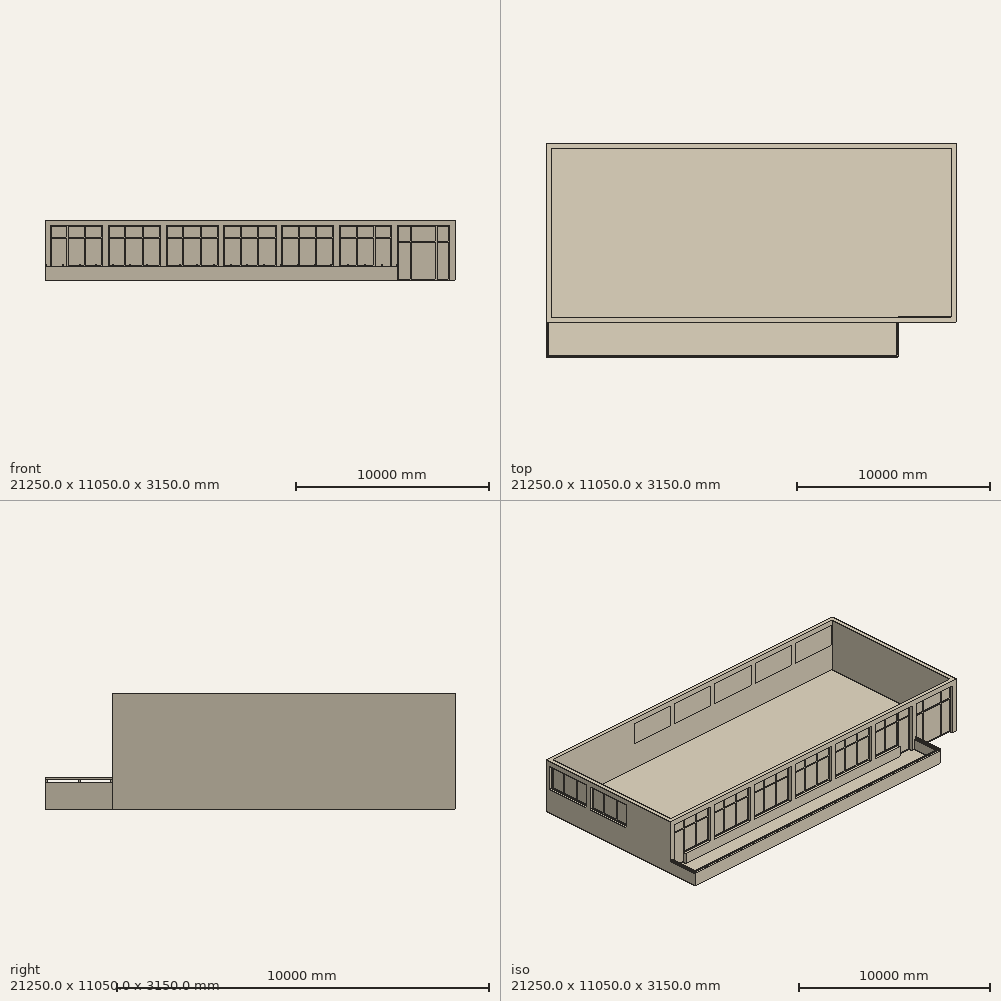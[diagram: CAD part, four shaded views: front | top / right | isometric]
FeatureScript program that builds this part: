
annotation { "Feature Type Name" : "Feature", "Feature Type Description" : "" }
export const myFeature = defineFeature(function(context is Context, id is Id, definition is map)
    precondition{}
    {
        {
            var Q0;
            Q0=qCreatedBy(makeId("Top.planeOp"),FACE);
            var sketch = newSketch(context, id + "F0", { "sketchPlane" : qUnion([Q0])});
            skLineSegment(sketch, "E0.bottom", {"start": v(0, 0) * mm, "end": v(21250, 0) * mm});
            skLineSegment(sketch, "E0.top", {"start": v(0, -9250) * mm, "end": v(21250, -9250) * mm});
            skLineSegment(sketch, "E0.left", {"start": v(0, 0) * mm, "end": v(0, -9250) * mm});
            skLineSegment(sketch, "E0.right", {"start": v(21250, 0) * mm, "end": v(21250, -9250) * mm});
            skSolve(sketch);
        }
        {
            var Q0;
            Q0=qSketchRegion(id+"F0",true);
            extrude(context, id + "F1", {"entities" : qUnion([Q0]), "depth" : 150 * mm, "offsetDistance" : 25 * mm});
        }
        {
            var Q0;
            Q0=makeQuery(id+"F1.opExtrude","CAP_FACE",FACE,{"disambiguationData":[OSD([sQuery(id+"F0.wireOp",EDGE,"E0.bottom"),sQuery(id+"F0.wireOp",EDGE,"E0.top"),sQuery(id+"F0.wireOp",EDGE,"E0.left"),sQuery(id+"F0.wireOp",EDGE,"E0.right")])],"isStart":false});
            var sketch = newSketch(context, id + "F2", { "sketchPlane" : qUnion([Q0])});
            skLineSegment(sketch, "E1.0.0", {"start": v(0, 0) * mm, "end": v(0, -9250) * mm});
            skLineSegment(sketch, "E1.0.1", {"start": v(0, -9250) * mm, "end": v(21250, -9250) * mm});
            skLineSegment(sketch, "E1.0.2", {"start": v(21250, -9250) * mm, "end": v(21250, 0) * mm});
            skLineSegment(sketch, "E1.0.3", {"start": v(21250, 0) * mm, "end": v(0, 0) * mm});
            skLineSegment(sketch, "E2.0", {"start": v(250, -250) * mm, "end": v(250, -9000) * mm});
            skLineSegment(sketch, "E2.1", {"start": v(21000, -250) * mm, "end": v(250, -250) * mm});
            skLineSegment(sketch, "E2.2", {"start": v(21000, -9000) * mm, "end": v(21000, -250) * mm});
            skLineSegment(sketch, "E2.3", {"start": v(250, -9000) * mm, "end": v(21000, -9000) * mm});
            skSolve(sketch);
        }
        {
            var Q0;
            Q0=qSketchRegion(id+"F2",true);
            extrude(context, id + "F3", {"entities" : qUnion([Q0]), "operationType" : NewBodyOperationType.ADD, "depth" : 3000 * mm, "offsetDistance" : 25 * mm});
        }
        {
            var Q0;
            Q0=makeQuery(id+"F3.boolean.opBoolean","MERGE",FACE,{"derivedFrom":[makeQuery(id+"F1.opExtrude","SWEPT_FACE",FACE,{"disambiguationData":[OSD([sQuery(id+"F0.wireOp",EDGE,"E0.top")])]}),makeQuery(id+"F3.opExtrude","SWEPT_FACE",FACE,{"disambiguationData":[OSD([sQuery(id+"F2.wireOp",EDGE,"E1.0.1")])]})]});
            var sketch = newSketch(context, id + "F4", { "sketchPlane" : qUnion([Q0])});
            skLineSegment(sketch, "E3", {"start": v(1150, 150) * mm, "end": v(250, 150) * mm});
            skLineSegment(sketch, "E4", {"start": v(250, 150) * mm, "end": v(250, 2850) * mm});
            skLineSegment(sketch, "E5", {"start": v(250, 2850) * mm, "end": v(2950, 2850) * mm});
            skLineSegment(sketch, "E6", {"start": v(2950, 2850) * mm, "end": v(2950, 750) * mm});
            skLineSegment(sketch, "E7", {"start": v(2950, 750) * mm, "end": v(1150, 750) * mm});
            skLineSegment(sketch, "E8", {"start": v(1150, 750) * mm, "end": v(1150, 150) * mm});
            skLineSegment(sketch, "E9.bottom", {"start": v(3250, 2850) * mm, "end": v(5950, 2850) * mm});
            skLineSegment(sketch, "E9.top", {"start": v(3250, 750) * mm, "end": v(5950, 750) * mm});
            skLineSegment(sketch, "E9.left", {"start": v(3250, 2850) * mm, "end": v(3250, 750) * mm});
            skLineSegment(sketch, "E9.right", {"start": v(5950, 2850) * mm, "end": v(5950, 750) * mm});
            skLineSegment(sketch, "E10.1.0.0", {"start": v(6250, 750) * mm, "end": v(8950, 750) * mm});
            skLineSegment(sketch, "E10.1.0.1", {"start": v(8950, 2850) * mm, "end": v(8950, 750) * mm});
            skLineSegment(sketch, "E10.1.0.2", {"start": v(6250, 2850) * mm, "end": v(6250, 750) * mm});
            skLineSegment(sketch, "E10.1.0.3", {"start": v(6250, 2850) * mm, "end": v(8950, 2850) * mm});
            skLineSegment(sketch, "E10.2.0.0", {"start": v(9250, 750) * mm, "end": v(11950, 750) * mm});
            skLineSegment(sketch, "E10.2.0.1", {"start": v(11950, 2850) * mm, "end": v(11950, 750) * mm});
            skLineSegment(sketch, "E10.2.0.2", {"start": v(9250, 2850) * mm, "end": v(9250, 750) * mm});
            skLineSegment(sketch, "E10.2.0.3", {"start": v(9250, 2850) * mm, "end": v(11950, 2850) * mm});
            skLineSegment(sketch, "E10.3.0.0", {"start": v(12250, 750) * mm, "end": v(14950, 750) * mm});
            skLineSegment(sketch, "E10.3.0.1", {"start": v(14950, 2850) * mm, "end": v(14950, 750) * mm});
            skLineSegment(sketch, "E10.3.0.2", {"start": v(12250, 2850) * mm, "end": v(12250, 750) * mm});
            skLineSegment(sketch, "E10.3.0.3", {"start": v(12250, 2850) * mm, "end": v(14950, 2850) * mm});
            skLineSegment(sketch, "E10.direction1", {"start": v(3250, 750) * mm, "end": v(6250, 750) * mm, "construction": true});
            skLineSegment(sketch, "E11.bottom", {"start": v(18250, 2850) * mm, "end": v(20950, 2850) * mm});
            skLineSegment(sketch, "E11.top", {"start": v(18250, 0) * mm, "end": v(20950, 0) * mm});
            skLineSegment(sketch, "E11.left", {"start": v(18250, 2850) * mm, "end": v(18250, 0) * mm});
            skLineSegment(sketch, "E11.right", {"start": v(20950, 2850) * mm, "end": v(20950, 0) * mm});
            skLineSegment(sketch, "E12", {"start": v(3250, 750) * mm, "end": v(14950, 750) * mm, "construction": true});
            skLineSegment(sketch, "E13", {"start": v(9100, 750) * mm, "end": v(9100, 3150) * mm, "construction": true});
            skLineSegment(sketch, "E14.MirrorCS", {"start": v(15250, 750) * mm, "end": v(17050, 750) * mm});
            skLineSegment(sketch, "E15.MirrorCS", {"start": v(17950, 2850) * mm, "end": v(15250, 2850) * mm});
            skLineSegment(sketch, "E16.MirrorCS", {"start": v(15250, 2850) * mm, "end": v(15250, 750) * mm});
            skLineSegment(sketch, "E17.MirrorCS", {"start": v(17050, 150) * mm, "end": v(17950, 150) * mm});
            skLineSegment(sketch, "E18.MirrorCS", {"start": v(17950, 150) * mm, "end": v(17950, 2850) * mm});
            skLineSegment(sketch, "E19.MirrorCS", {"start": v(17050, 750) * mm, "end": v(17050, 150) * mm});
            skSolve(sketch);
        }
        {
            var Q0;
            Q0=qSketchRegion(id+"F4",true);
            extrude(context, id + "F5", {"entities" : qUnion([Q0]), "operationType" : NewBodyOperationType.REMOVE, "oppositeDirection" : true, "depth" : 300 * mm, "offsetDistance" : 25 * mm});
        }
        {
            var Q0;
            Q0=makeQuery(id+"F3.opExtrude","SWEPT_FACE",FACE,{"disambiguationData":[OSD([sQuery(id+"F2.wireOp",EDGE,"E2.3")])]});
            var sketch = newSketch(context, id + "F6", { "sketchPlane" : qUnion([Q0])});
            skLineSegment(sketch, "E20.0", {"start": v(-1150, 150) * mm, "end": v(-250, 150) * mm});
            skLineSegment(sketch, "E20.1", {"start": v(-250, 150) * mm, "end": v(-250, 2850) * mm});
            skLineSegment(sketch, "E20.2", {"start": v(-250, 2850) * mm, "end": v(-2950, 2850) * mm});
            skLineSegment(sketch, "E20.3", {"start": v(-2950, 2850) * mm, "end": v(-2950, 750) * mm});
            skLineSegment(sketch, "E20.4", {"start": v(-2950, 750) * mm, "end": v(-1150, 750) * mm});
            skLineSegment(sketch, "E20.5", {"start": v(-1150, 750) * mm, "end": v(-1150, 150) * mm});
            skLineSegment(sketch, "E20.6", {"start": v(-3250, 2850) * mm, "end": v(-5950, 2850) * mm});
            skLineSegment(sketch, "E20.7", {"start": v(-3250, 750) * mm, "end": v(-5950, 750) * mm});
            skLineSegment(sketch, "E20.8", {"start": v(-3250, 2850) * mm, "end": v(-3250, 750) * mm});
            skLineSegment(sketch, "E20.9", {"start": v(-5950, 2850) * mm, "end": v(-5950, 750) * mm});
            skLineSegment(sketch, "E20.10", {"start": v(-6250, 750) * mm, "end": v(-8950, 750) * mm});
            skLineSegment(sketch, "E20.11", {"start": v(-8950, 2850) * mm, "end": v(-8950, 750) * mm});
            skLineSegment(sketch, "E20.12", {"start": v(-6250, 2850) * mm, "end": v(-6250, 750) * mm});
            skLineSegment(sketch, "E20.13", {"start": v(-6250, 2850) * mm, "end": v(-8950, 2850) * mm});
            skLineSegment(sketch, "E20.14", {"start": v(-9250, 750) * mm, "end": v(-11950, 750) * mm});
            skLineSegment(sketch, "E20.15", {"start": v(-11950, 2850) * mm, "end": v(-11950, 750) * mm});
            skLineSegment(sketch, "E20.16", {"start": v(-9250, 2850) * mm, "end": v(-9250, 750) * mm});
            skLineSegment(sketch, "E20.17", {"start": v(-9250, 2850) * mm, "end": v(-11950, 2850) * mm});
            skLineSegment(sketch, "E20.18", {"start": v(-12250, 750) * mm, "end": v(-14950, 750) * mm});
            skLineSegment(sketch, "E20.19", {"start": v(-14950, 2850) * mm, "end": v(-14950, 750) * mm});
            skLineSegment(sketch, "E20.20", {"start": v(-12250, 2850) * mm, "end": v(-12250, 750) * mm});
            skLineSegment(sketch, "E20.21", {"start": v(-12250, 2850) * mm, "end": v(-14950, 2850) * mm});
            skLineSegment(sketch, "E20.26", {"start": v(-3250, 750) * mm, "end": v(-6250, 750) * mm});
            skLineSegment(sketch, "E20.27", {"start": v(-18250, 2850) * mm, "end": v(-20950, 2850) * mm});
            skLineSegment(sketch, "E20.28", {"start": v(-18250, 0) * mm, "end": v(-20950, 0) * mm});
            skLineSegment(sketch, "E20.29", {"start": v(-18250, 2850) * mm, "end": v(-18250, 0) * mm});
            skLineSegment(sketch, "E20.30", {"start": v(-20950, 2850) * mm, "end": v(-20950, 0) * mm});
            skLineSegment(sketch, "E21.0", {"start": v(-17950, 2850) * mm, "end": v(-15250, 2850) * mm});
            skLineSegment(sketch, "E22.0", {"start": v(-15250, 2850) * mm, "end": v(-15250, 750) * mm});
            skLineSegment(sketch, "E23.0", {"start": v(-15250, 750) * mm, "end": v(-17050, 750) * mm});
            skLineSegment(sketch, "E24.0", {"start": v(-17050, 750) * mm, "end": v(-17050, 150) * mm});
            skLineSegment(sketch, "E25.0", {"start": v(-17050, 150) * mm, "end": v(-17950, 150) * mm});
            skLineSegment(sketch, "E26.0", {"start": v(-17950, 150) * mm, "end": v(-17950, 2850) * mm});
            skSolve(sketch);
        }
        {
            var Q0;
            Q0=qSketchRegion(id+"F6",true);
            extrude(context, id + "F7", {"entities" : qUnion([Q0]), "oppositeDirection" : true, "depth" : 50 * mm, "offsetDistance" : 25 * mm});
        }
        {
            var Q0;
            Q0=makeQuery(id+"F7.opExtrude","CAP_FACE",FACE,{"disambiguationData":[OSD([sQuery(id+"F6.wireOp",EDGE,"E20.0"),sQuery(id+"F6.wireOp",EDGE,"E20.1"),sQuery(id+"F6.wireOp",EDGE,"E20.2"),sQuery(id+"F6.wireOp",EDGE,"E20.3"),sQuery(id+"F6.wireOp",EDGE,"E20.4"),sQuery(id+"F6.wireOp",EDGE,"E20.5")])],"isStart":false});
            var sketch = newSketch(context, id + "F8", { "sketchPlane" : qUnion([Q0])});
            skLineSegment(sketch, "E27.bottom", {"start": v(300, 2200) * mm, "end": v(1112.5, 2200) * mm});
            skLineSegment(sketch, "E27.top", {"start": v(300, 200) * mm, "end": v(1112.5, 200) * mm});
            skLineSegment(sketch, "E27.left", {"start": v(300, 2200) * mm, "end": v(300, 200) * mm});
            skLineSegment(sketch, "E27.right", {"start": v(1112.5, 2200) * mm, "end": v(1112.5, 200) * mm});
            skLineSegment(sketch, "E28.bottom", {"start": v(300, 2250) * mm, "end": v(1112.5, 2250) * mm});
            skLineSegment(sketch, "E28.top", {"start": v(300, 2800) * mm, "end": v(1112.5, 2800) * mm});
            skLineSegment(sketch, "E28.left", {"start": v(300, 2250) * mm, "end": v(300, 2800) * mm});
            skLineSegment(sketch, "E28.right", {"start": v(1112.5, 2250) * mm, "end": v(1112.5, 2800) * mm});
            skLineSegment(sketch, "E29.0.0", {"start": v(250, 150) * mm, "end": v(1150, 150) * mm});
            skLineSegment(sketch, "E29.0.1", {"start": v(1150, 150) * mm, "end": v(1150, 750) * mm});
            skLineSegment(sketch, "E29.0.2", {"start": v(1150, 750) * mm, "end": v(2950, 750) * mm});
            skLineSegment(sketch, "E29.0.3", {"start": v(2950, 750) * mm, "end": v(2950, 2850) * mm});
            skLineSegment(sketch, "E29.0.4", {"start": v(2950, 2850) * mm, "end": v(250, 2850) * mm});
            skLineSegment(sketch, "E29.0.5", {"start": v(250, 2850) * mm, "end": v(250, 150) * mm});
            skLineSegment(sketch, "E30.bottom", {"start": v(1187.5, 2800) * mm, "end": v(2037.5, 2800) * mm});
            skLineSegment(sketch, "E30.top", {"start": v(1187.5, 2250) * mm, "end": v(2037.5, 2250) * mm});
            skLineSegment(sketch, "E30.left", {"start": v(1187.5, 2800) * mm, "end": v(1187.5, 2250) * mm});
            skLineSegment(sketch, "E30.right", {"start": v(2037.5, 2800) * mm, "end": v(2037.5, 2250) * mm});
            skLineSegment(sketch, "E31.bottom", {"start": v(2087.5, 2800) * mm, "end": v(2900, 2800) * mm});
            skLineSegment(sketch, "E31.top", {"start": v(2087.5, 2250) * mm, "end": v(2900, 2250) * mm});
            skLineSegment(sketch, "E31.left", {"start": v(2087.5, 2800) * mm, "end": v(2087.5, 2250) * mm});
            skLineSegment(sketch, "E31.right", {"start": v(2900, 2800) * mm, "end": v(2900, 2250) * mm});
            skLineSegment(sketch, "E32.bottom", {"start": v(1187.5, 2200) * mm, "end": v(2037.5, 2200) * mm});
            skLineSegment(sketch, "E32.top", {"start": v(1187.5, 800) * mm, "end": v(2037.5, 800) * mm});
            skLineSegment(sketch, "E32.left", {"start": v(1187.5, 2200) * mm, "end": v(1187.5, 800) * mm});
            skLineSegment(sketch, "E32.right", {"start": v(2037.5, 2200) * mm, "end": v(2037.5, 800) * mm});
            skLineSegment(sketch, "E33.bottom", {"start": v(2087.5, 2200) * mm, "end": v(2900, 2200) * mm});
            skLineSegment(sketch, "E33.top", {"start": v(2087.5, 800) * mm, "end": v(2900, 800) * mm});
            skLineSegment(sketch, "E33.left", {"start": v(2087.5, 2200) * mm, "end": v(2087.5, 800) * mm});
            skLineSegment(sketch, "E33.right", {"start": v(2900, 2200) * mm, "end": v(2900, 800) * mm});
            skLineSegment(sketch, "E34.bottom", {"start": v(3300, 2250) * mm, "end": v(4112.5, 2250) * mm});
            skLineSegment(sketch, "E34.top", {"start": v(3300, 2800) * mm, "end": v(4112.5, 2800) * mm});
            skLineSegment(sketch, "E34.left", {"start": v(3300, 2250) * mm, "end": v(3300, 2800) * mm});
            skLineSegment(sketch, "E34.right", {"start": v(4112.5, 2250) * mm, "end": v(4112.5, 2800) * mm});
            skLineSegment(sketch, "E35.bottom", {"start": v(4162.5, 2800) * mm, "end": v(5012.5, 2800) * mm});
            skLineSegment(sketch, "E35.top", {"start": v(4162.5, 2250) * mm, "end": v(5012.5, 2250) * mm});
            skLineSegment(sketch, "E35.left", {"start": v(4162.5, 2800) * mm, "end": v(4162.5, 2250) * mm});
            skLineSegment(sketch, "E35.right", {"start": v(5012.5, 2800) * mm, "end": v(5012.5, 2250) * mm});
            skLineSegment(sketch, "E36.bottom", {"start": v(5062.5, 2800) * mm, "end": v(5900, 2800) * mm});
            skLineSegment(sketch, "E36.top", {"start": v(5062.5, 2250) * mm, "end": v(5900, 2250) * mm});
            skLineSegment(sketch, "E36.left", {"start": v(5062.5, 2800) * mm, "end": v(5062.5, 2250) * mm});
            skLineSegment(sketch, "E36.right", {"start": v(5900, 2800) * mm, "end": v(5900, 2250) * mm});
            skLineSegment(sketch, "E37.bottom", {"start": v(4162.5, 2200) * mm, "end": v(5012.5, 2200) * mm});
            skLineSegment(sketch, "E37.top", {"start": v(4162.5, 800) * mm, "end": v(5012.5, 800) * mm});
            skLineSegment(sketch, "E37.left", {"start": v(4162.5, 2200) * mm, "end": v(4162.5, 800) * mm});
            skLineSegment(sketch, "E37.right", {"start": v(5012.5, 2200) * mm, "end": v(5012.5, 800) * mm});
            skLineSegment(sketch, "E38.bottom", {"start": v(5062.5, 2200) * mm, "end": v(5900, 2200) * mm});
            skLineSegment(sketch, "E38.top", {"start": v(5062.5, 800) * mm, "end": v(5900, 800) * mm});
            skLineSegment(sketch, "E38.left", {"start": v(5062.5, 2200) * mm, "end": v(5062.5, 800) * mm});
            skLineSegment(sketch, "E38.right", {"start": v(5900, 2200) * mm, "end": v(5900, 800) * mm});
            skLineSegment(sketch, "E39.0.0", {"start": v(3250, 750) * mm, "end": v(5950, 750) * mm});
            skLineSegment(sketch, "E39.0.1", {"start": v(5950, 750) * mm, "end": v(5950, 2850) * mm});
            skLineSegment(sketch, "E39.0.2", {"start": v(5950, 2850) * mm, "end": v(3250, 2850) * mm});
            skLineSegment(sketch, "E39.0.3", {"start": v(3250, 2850) * mm, "end": v(3250, 750) * mm});
            skLineSegment(sketch, "E40.bottom", {"start": v(4112.5, 2200) * mm, "end": v(3300, 2200) * mm});
            skLineSegment(sketch, "E40.top", {"start": v(4112.5, 800) * mm, "end": v(3300, 800) * mm});
            skLineSegment(sketch, "E40.left", {"start": v(4112.5, 2200) * mm, "end": v(4112.5, 800) * mm});
            skLineSegment(sketch, "E40.right", {"start": v(3300, 2200) * mm, "end": v(3300, 800) * mm});
            skLineSegment(sketch, "E41.1.0.0", {"start": v(8062.5, 2800) * mm, "end": v(8900, 2800) * mm});
            skLineSegment(sketch, "E41.1.0.1", {"start": v(7112.5, 2200) * mm, "end": v(6300, 2200) * mm});
            skLineSegment(sketch, "E41.1.0.2", {"start": v(6300, 2800) * mm, "end": v(7112.5, 2800) * mm});
            skLineSegment(sketch, "E41.1.0.3", {"start": v(8062.5, 800) * mm, "end": v(8900, 800) * mm});
            skLineSegment(sketch, "E41.1.0.4", {"start": v(6300, 2200) * mm, "end": v(6300, 800) * mm});
            skLineSegment(sketch, "E41.1.0.5", {"start": v(7162.5, 2800) * mm, "end": v(8012.5, 2800) * mm});
            skLineSegment(sketch, "E41.1.0.6", {"start": v(6250, 750) * mm, "end": v(8950, 750) * mm});
            skLineSegment(sketch, "E41.1.0.7", {"start": v(8900, 2800) * mm, "end": v(8900, 2250) * mm});
            skLineSegment(sketch, "E41.1.0.8", {"start": v(7162.5, 2200) * mm, "end": v(8012.5, 2200) * mm});
            skLineSegment(sketch, "E41.1.0.9", {"start": v(8950, 750) * mm, "end": v(8950, 2850) * mm});
            skLineSegment(sketch, "E41.1.0.10", {"start": v(7162.5, 2250) * mm, "end": v(8012.5, 2250) * mm});
            skLineSegment(sketch, "E41.1.0.11", {"start": v(8062.5, 2800) * mm, "end": v(8062.5, 2250) * mm});
            skLineSegment(sketch, "E41.1.0.12", {"start": v(7112.5, 2200) * mm, "end": v(7112.5, 800) * mm});
            skLineSegment(sketch, "E41.1.0.13", {"start": v(8062.5, 2200) * mm, "end": v(8062.5, 800) * mm});
            skLineSegment(sketch, "E41.1.0.14", {"start": v(6300, 2250) * mm, "end": v(6300, 2800) * mm});
            skLineSegment(sketch, "E41.1.0.15", {"start": v(7162.5, 800) * mm, "end": v(8012.5, 800) * mm});
            skLineSegment(sketch, "E41.1.0.16", {"start": v(8012.5, 2200) * mm, "end": v(8012.5, 800) * mm});
            skLineSegment(sketch, "E41.1.0.17", {"start": v(8950, 2850) * mm, "end": v(6250, 2850) * mm});
            skLineSegment(sketch, "E41.1.0.18", {"start": v(7162.5, 2800) * mm, "end": v(7162.5, 2250) * mm});
            skLineSegment(sketch, "E41.1.0.19", {"start": v(7112.5, 800) * mm, "end": v(6300, 800) * mm});
            skLineSegment(sketch, "E41.1.0.20", {"start": v(8062.5, 2250) * mm, "end": v(8900, 2250) * mm});
            skLineSegment(sketch, "E41.1.0.21", {"start": v(8900, 2200) * mm, "end": v(8900, 800) * mm});
            skLineSegment(sketch, "E41.1.0.22", {"start": v(7112.5, 2250) * mm, "end": v(7112.5, 2800) * mm});
            skLineSegment(sketch, "E41.1.0.23", {"start": v(7162.5, 2200) * mm, "end": v(7162.5, 800) * mm});
            skLineSegment(sketch, "E41.1.0.24", {"start": v(6250, 2850) * mm, "end": v(6250, 750) * mm});
            skLineSegment(sketch, "E41.1.0.25", {"start": v(8062.5, 2200) * mm, "end": v(8900, 2200) * mm});
            skLineSegment(sketch, "E41.1.0.26", {"start": v(8012.5, 2800) * mm, "end": v(8012.5, 2250) * mm});
            skLineSegment(sketch, "E41.1.0.27", {"start": v(6300, 2250) * mm, "end": v(7112.5, 2250) * mm});
            skLineSegment(sketch, "E41.2.0.0", {"start": v(11062.5, 2800) * mm, "end": v(11900, 2800) * mm});
            skLineSegment(sketch, "E41.2.0.1", {"start": v(10112.5, 2200) * mm, "end": v(9300, 2200) * mm});
            skLineSegment(sketch, "E41.2.0.2", {"start": v(9300, 2800) * mm, "end": v(10112.5, 2800) * mm});
            skLineSegment(sketch, "E41.2.0.3", {"start": v(11062.5, 800) * mm, "end": v(11900, 800) * mm});
            skLineSegment(sketch, "E41.2.0.4", {"start": v(9300, 2200) * mm, "end": v(9300, 800) * mm});
            skLineSegment(sketch, "E41.2.0.5", {"start": v(10162.5, 2800) * mm, "end": v(11012.5, 2800) * mm});
            skLineSegment(sketch, "E41.2.0.6", {"start": v(9250, 750) * mm, "end": v(11950, 750) * mm});
            skLineSegment(sketch, "E41.2.0.7", {"start": v(11900, 2800) * mm, "end": v(11900, 2250) * mm});
            skLineSegment(sketch, "E41.2.0.8", {"start": v(10162.5, 2200) * mm, "end": v(11012.5, 2200) * mm});
            skLineSegment(sketch, "E41.2.0.9", {"start": v(11950, 750) * mm, "end": v(11950, 2850) * mm});
            skLineSegment(sketch, "E41.2.0.10", {"start": v(10162.5, 2250) * mm, "end": v(11012.5, 2250) * mm});
            skLineSegment(sketch, "E41.2.0.11", {"start": v(11062.5, 2800) * mm, "end": v(11062.5, 2250) * mm});
            skLineSegment(sketch, "E41.2.0.12", {"start": v(10112.5, 2200) * mm, "end": v(10112.5, 800) * mm});
            skLineSegment(sketch, "E41.2.0.13", {"start": v(11062.5, 2200) * mm, "end": v(11062.5, 800) * mm});
            skLineSegment(sketch, "E41.2.0.14", {"start": v(9300, 2250) * mm, "end": v(9300, 2800) * mm});
            skLineSegment(sketch, "E41.2.0.15", {"start": v(10162.5, 800) * mm, "end": v(11012.5, 800) * mm});
            skLineSegment(sketch, "E41.2.0.16", {"start": v(11012.5, 2200) * mm, "end": v(11012.5, 800) * mm});
            skLineSegment(sketch, "E41.2.0.17", {"start": v(11950, 2850) * mm, "end": v(9250, 2850) * mm});
            skLineSegment(sketch, "E41.2.0.18", {"start": v(10162.5, 2800) * mm, "end": v(10162.5, 2250) * mm});
            skLineSegment(sketch, "E41.2.0.19", {"start": v(10112.5, 800) * mm, "end": v(9300, 800) * mm});
            skLineSegment(sketch, "E41.2.0.20", {"start": v(11062.5, 2250) * mm, "end": v(11900, 2250) * mm});
            skLineSegment(sketch, "E41.2.0.21", {"start": v(11900, 2200) * mm, "end": v(11900, 800) * mm});
            skLineSegment(sketch, "E41.2.0.22", {"start": v(10112.5, 2250) * mm, "end": v(10112.5, 2800) * mm});
            skLineSegment(sketch, "E41.2.0.23", {"start": v(10162.5, 2200) * mm, "end": v(10162.5, 800) * mm});
            skLineSegment(sketch, "E41.2.0.24", {"start": v(9250, 2850) * mm, "end": v(9250, 750) * mm});
            skLineSegment(sketch, "E41.2.0.25", {"start": v(11062.5, 2200) * mm, "end": v(11900, 2200) * mm});
            skLineSegment(sketch, "E41.2.0.26", {"start": v(11012.5, 2800) * mm, "end": v(11012.5, 2250) * mm});
            skLineSegment(sketch, "E41.2.0.27", {"start": v(9300, 2250) * mm, "end": v(10112.5, 2250) * mm});
            skLineSegment(sketch, "E41.3.0.0", {"start": v(14062.5, 2800) * mm, "end": v(14900, 2800) * mm});
            skLineSegment(sketch, "E41.3.0.1", {"start": v(13112.5, 2200) * mm, "end": v(12300, 2200) * mm});
            skLineSegment(sketch, "E41.3.0.2", {"start": v(12300, 2800) * mm, "end": v(13112.5, 2800) * mm});
            skLineSegment(sketch, "E41.3.0.3", {"start": v(14062.5, 800) * mm, "end": v(14900, 800) * mm});
            skLineSegment(sketch, "E41.3.0.4", {"start": v(12300, 2200) * mm, "end": v(12300, 800) * mm});
            skLineSegment(sketch, "E41.3.0.5", {"start": v(13162.5, 2800) * mm, "end": v(14012.5, 2800) * mm});
            skLineSegment(sketch, "E41.3.0.6", {"start": v(12250, 750) * mm, "end": v(14950, 750) * mm});
            skLineSegment(sketch, "E41.3.0.7", {"start": v(14900, 2800) * mm, "end": v(14900, 2250) * mm});
            skLineSegment(sketch, "E41.3.0.8", {"start": v(13162.5, 2200) * mm, "end": v(14012.5, 2200) * mm});
            skLineSegment(sketch, "E41.3.0.9", {"start": v(14950, 750) * mm, "end": v(14950, 2850) * mm});
            skLineSegment(sketch, "E41.3.0.10", {"start": v(13162.5, 2250) * mm, "end": v(14012.5, 2250) * mm});
            skLineSegment(sketch, "E41.3.0.11", {"start": v(14062.5, 2800) * mm, "end": v(14062.5, 2250) * mm});
            skLineSegment(sketch, "E41.3.0.12", {"start": v(13112.5, 2200) * mm, "end": v(13112.5, 800) * mm});
            skLineSegment(sketch, "E41.3.0.13", {"start": v(14062.5, 2200) * mm, "end": v(14062.5, 800) * mm});
            skLineSegment(sketch, "E41.3.0.14", {"start": v(12300, 2250) * mm, "end": v(12300, 2800) * mm});
            skLineSegment(sketch, "E41.3.0.15", {"start": v(13162.5, 800) * mm, "end": v(14012.5, 800) * mm});
            skLineSegment(sketch, "E41.3.0.16", {"start": v(14012.5, 2200) * mm, "end": v(14012.5, 800) * mm});
            skLineSegment(sketch, "E41.3.0.17", {"start": v(14950, 2850) * mm, "end": v(12250, 2850) * mm});
            skLineSegment(sketch, "E41.3.0.18", {"start": v(13162.5, 2800) * mm, "end": v(13162.5, 2250) * mm});
            skLineSegment(sketch, "E41.3.0.19", {"start": v(13112.5, 800) * mm, "end": v(12300, 800) * mm});
            skLineSegment(sketch, "E41.3.0.20", {"start": v(14062.5, 2250) * mm, "end": v(14900, 2250) * mm});
            skLineSegment(sketch, "E41.3.0.21", {"start": v(14900, 2200) * mm, "end": v(14900, 800) * mm});
            skLineSegment(sketch, "E41.3.0.22", {"start": v(13112.5, 2250) * mm, "end": v(13112.5, 2800) * mm});
            skLineSegment(sketch, "E41.3.0.23", {"start": v(13162.5, 2200) * mm, "end": v(13162.5, 800) * mm});
            skLineSegment(sketch, "E41.3.0.24", {"start": v(12250, 2850) * mm, "end": v(12250, 750) * mm});
            skLineSegment(sketch, "E41.3.0.25", {"start": v(14062.5, 2200) * mm, "end": v(14900, 2200) * mm});
            skLineSegment(sketch, "E41.3.0.26", {"start": v(14012.5, 2800) * mm, "end": v(14012.5, 2250) * mm});
            skLineSegment(sketch, "E41.3.0.27", {"start": v(12300, 2250) * mm, "end": v(13112.5, 2250) * mm});
            skLineSegment(sketch, "E41.direction1", {"start": v(3250, 750) * mm, "end": v(6250, 750) * mm, "construction": true});
            skLineSegment(sketch, "E42.bottom", {"start": v(18975, 2800) * mm, "end": v(20225, 2800) * mm});
            skLineSegment(sketch, "E42.top", {"start": v(18975, 50) * mm, "end": v(20225, 50) * mm});
            skLineSegment(sketch, "E42.left", {"start": v(18975, 2800) * mm, "end": v(18975, 2050) * mm});
            skLineSegment(sketch, "E42.right", {"start": v(20225, 2800) * mm, "end": v(20225, 2050) * mm});
            skLineSegment(sketch, "E43.bottom", {"start": v(18300, 2800) * mm, "end": v(18900, 2800) * mm});
            skLineSegment(sketch, "E43.top", {"start": v(18300, 50) * mm, "end": v(18900, 50) * mm});
            skLineSegment(sketch, "E43.left", {"start": v(18300, 2800) * mm, "end": v(18300, 2050) * mm});
            skLineSegment(sketch, "E43.right", {"start": v(18900, 2800) * mm, "end": v(18900, 2050) * mm});
            skLineSegment(sketch, "E44.bottom", {"start": v(20300, 2800) * mm, "end": v(20900, 2800) * mm});
            skLineSegment(sketch, "E44.top", {"start": v(20300, 50) * mm, "end": v(20900, 50) * mm});
            skLineSegment(sketch, "E44.left", {"start": v(20300, 2800) * mm, "end": v(20300, 2050) * mm});
            skLineSegment(sketch, "E44.right", {"start": v(20900, 2800) * mm, "end": v(20900, 2050) * mm});
            skLineSegment(sketch, "E45", {"start": v(18300, 2050) * mm, "end": v(18900, 2050) * mm});
            skLineSegment(sketch, "E46", {"start": v(18300, 2000) * mm, "end": v(18900, 2000) * mm});
            skLineSegment(sketch, "E47.trimOffspring", {"start": v(18300, 2000) * mm, "end": v(18300, 50) * mm});
            skLineSegment(sketch, "E48.trimOffspring", {"start": v(18900, 2000) * mm, "end": v(18900, 50) * mm});
            skLineSegment(sketch, "E49.trimOffspring", {"start": v(18975, 2050) * mm, "end": v(20225, 2050) * mm});
            skLineSegment(sketch, "E50.trimOffspring", {"start": v(18975, 2000) * mm, "end": v(18975, 50) * mm});
            skLineSegment(sketch, "E51.trimOffspring", {"start": v(18975, 2000) * mm, "end": v(20225, 2000) * mm});
            skLineSegment(sketch, "E52.trimOffspring", {"start": v(20300, 2050) * mm, "end": v(20900, 2050) * mm});
            skLineSegment(sketch, "E53.trimOffspring", {"start": v(20300, 2000) * mm, "end": v(20300, 50) * mm});
            skLineSegment(sketch, "E54.trimOffspring", {"start": v(20300, 2000) * mm, "end": v(20900, 2000) * mm});
            skLineSegment(sketch, "E55.trimOffspring", {"start": v(20225, 2000) * mm, "end": v(20225, 50) * mm});
            skLineSegment(sketch, "E56.trimOffspring", {"start": v(20900, 2000) * mm, "end": v(20900, 50) * mm});
            skLineSegment(sketch, "E57.0.0", {"start": v(18250, 0) * mm, "end": v(20950, 0) * mm});
            skLineSegment(sketch, "E57.0.1", {"start": v(20950, 0) * mm, "end": v(20950, 2850) * mm});
            skLineSegment(sketch, "E57.0.2", {"start": v(20950, 2850) * mm, "end": v(18250, 2850) * mm});
            skLineSegment(sketch, "E57.0.3", {"start": v(18250, 2850) * mm, "end": v(18250, 0) * mm});
            skLineSegment(sketch, "E58", {"start": v(3250, 750) * mm, "end": v(14950, 750) * mm, "construction": true});
            skLineSegment(sketch, "E59", {"start": v(9100, 750) * mm, "end": v(9100, 3041.44) * mm, "construction": true});
            skLineSegment(sketch, "E60.MirrorCS", {"start": v(17012.5, 2250) * mm, "end": v(16162.5, 2250) * mm});
            skLineSegment(sketch, "E61.MirrorCS", {"start": v(17900, 2200) * mm, "end": v(17087.5, 2200) * mm});
            skLineSegment(sketch, "E62.MirrorCS", {"start": v(16112.5, 2200) * mm, "end": v(15300, 2200) * mm});
            skLineSegment(sketch, "E63.MirrorCS", {"start": v(15250, 750) * mm, "end": v(15250, 2850) * mm});
            skLineSegment(sketch, "E64.MirrorCS", {"start": v(16112.5, 800) * mm, "end": v(15300, 800) * mm});
            skLineSegment(sketch, "E65.MirrorCS", {"start": v(17900, 200) * mm, "end": v(17087.5, 200) * mm});
            skLineSegment(sketch, "E66.MirrorCS", {"start": v(17012.5, 800) * mm, "end": v(16162.5, 800) * mm});
            skLineSegment(sketch, "E67.MirrorCS", {"start": v(16112.5, 2200) * mm, "end": v(16112.5, 800) * mm});
            skLineSegment(sketch, "E68.MirrorCS", {"start": v(17950, 2850) * mm, "end": v(17950, 150) * mm});
            skLineSegment(sketch, "E69.MirrorCS", {"start": v(16112.5, 2800) * mm, "end": v(15300, 2800) * mm});
            skLineSegment(sketch, "E70.MirrorCS", {"start": v(17012.5, 2200) * mm, "end": v(17012.5, 800) * mm});
            skLineSegment(sketch, "E71.MirrorCS", {"start": v(16112.5, 2250) * mm, "end": v(15300, 2250) * mm});
            skLineSegment(sketch, "E72.MirrorCS", {"start": v(15250, 2850) * mm, "end": v(17950, 2850) * mm});
            skLineSegment(sketch, "E73.MirrorCS", {"start": v(17950, 150) * mm, "end": v(17050, 150) * mm});
            skLineSegment(sketch, "E74.MirrorCS", {"start": v(17012.5, 2800) * mm, "end": v(16162.5, 2800) * mm});
            skLineSegment(sketch, "E75.MirrorCS", {"start": v(15300, 2200) * mm, "end": v(15300, 800) * mm});
            skLineSegment(sketch, "E76.MirrorCS", {"start": v(17900, 2250) * mm, "end": v(17087.5, 2250) * mm});
            skLineSegment(sketch, "E77.MirrorCS", {"start": v(17087.5, 2200) * mm, "end": v(17087.5, 200) * mm});
            skLineSegment(sketch, "E78.MirrorCS", {"start": v(17900, 2800) * mm, "end": v(17087.5, 2800) * mm});
            skLineSegment(sketch, "E79.MirrorCS", {"start": v(15300, 2800) * mm, "end": v(15300, 2250) * mm});
            skLineSegment(sketch, "E80.MirrorCS", {"start": v(17087.5, 2250) * mm, "end": v(17087.5, 2800) * mm});
            skLineSegment(sketch, "E81.MirrorCS", {"start": v(16112.5, 2800) * mm, "end": v(16112.5, 2250) * mm});
            skLineSegment(sketch, "E82.MirrorCS", {"start": v(17050, 750) * mm, "end": v(15250, 750) * mm});
            skLineSegment(sketch, "E83.MirrorCS", {"start": v(16162.5, 2800) * mm, "end": v(16162.5, 2250) * mm});
            skLineSegment(sketch, "E84.MirrorCS", {"start": v(17012.5, 2200) * mm, "end": v(16162.5, 2200) * mm});
            skLineSegment(sketch, "E85.MirrorCS", {"start": v(17050, 150) * mm, "end": v(17050, 750) * mm});
            skLineSegment(sketch, "E86.MirrorCS", {"start": v(17012.5, 2800) * mm, "end": v(17012.5, 2250) * mm});
            skLineSegment(sketch, "E87.MirrorCS", {"start": v(17900, 2250) * mm, "end": v(17900, 2800) * mm});
            skLineSegment(sketch, "E88.MirrorCS", {"start": v(17900, 2200) * mm, "end": v(17900, 200) * mm});
            skLineSegment(sketch, "E89.MirrorCS", {"start": v(16162.5, 2200) * mm, "end": v(16162.5, 800) * mm});
            skPoint(sketch, "E90.orphan", {"position": v(20950, 2150) * mm});
            skSolve(sketch);
        }
        {
            var Q0;
            Q0=qSketchRegion(id+"F8",true);
            extrude(context, id + "F9", {"entities" : qUnion([Q0]), "depth" : 25 * mm, "offsetDistance" : 25 * mm});
        }
        {
            var Q0;
            Q0=makeQuery(id+"F3.boolean.opBoolean","MERGE",FACE,{"derivedFrom":[makeQuery(id+"F1.opExtrude","SWEPT_FACE",FACE,{"disambiguationData":[OSD([sQuery(id+"F0.wireOp",EDGE,"E0.bottom")])]}),makeQuery(id+"F3.opExtrude","SWEPT_FACE",FACE,{"disambiguationData":[OSD([sQuery(id+"F2.wireOp",EDGE,"E1.0.3")])]})]});
            var sketch = newSketch(context, id + "F10", { "sketchPlane" : qUnion([Q0])});
            skLineSegment(sketch, "E91.bottom", {"start": v(-17975, 2850) * mm, "end": v(-15275, 2850) * mm});
            skLineSegment(sketch, "E91.top", {"start": v(-17975, 1650) * mm, "end": v(-15275, 1650) * mm});
            skLineSegment(sketch, "E91.left", {"start": v(-17975, 2850) * mm, "end": v(-17975, 1650) * mm});
            skLineSegment(sketch, "E91.right", {"start": v(-15275, 2850) * mm, "end": v(-15275, 1650) * mm});
            skLineSegment(sketch, "E92.1.0.0", {"start": v(-12275, 2850) * mm, "end": v(-12275, 1650) * mm});
            skLineSegment(sketch, "E92.1.0.1", {"start": v(-14975, 2850) * mm, "end": v(-14975, 1650) * mm});
            skLineSegment(sketch, "E92.1.0.2", {"start": v(-14975, 1650) * mm, "end": v(-12275, 1650) * mm});
            skLineSegment(sketch, "E92.1.0.3", {"start": v(-14975, 2850) * mm, "end": v(-12275, 2850) * mm});
            skLineSegment(sketch, "E92.2.0.0", {"start": v(-9275, 2850) * mm, "end": v(-9275, 1650) * mm});
            skLineSegment(sketch, "E92.2.0.1", {"start": v(-11975, 2850) * mm, "end": v(-11975, 1650) * mm});
            skLineSegment(sketch, "E92.2.0.2", {"start": v(-11975, 1650) * mm, "end": v(-9275, 1650) * mm});
            skLineSegment(sketch, "E92.2.0.3", {"start": v(-11975, 2850) * mm, "end": v(-9275, 2850) * mm});
            skLineSegment(sketch, "E92.3.0.0", {"start": v(-6275, 2850) * mm, "end": v(-6275, 1650) * mm});
            skLineSegment(sketch, "E92.3.0.1", {"start": v(-8975, 2850) * mm, "end": v(-8975, 1650) * mm});
            skLineSegment(sketch, "E92.3.0.2", {"start": v(-8975, 1650) * mm, "end": v(-6275, 1650) * mm});
            skLineSegment(sketch, "E92.3.0.3", {"start": v(-8975, 2850) * mm, "end": v(-6275, 2850) * mm});
            skLineSegment(sketch, "E92.direction1", {"start": v(-17975, 1650) * mm, "end": v(-14975, 1650) * mm, "construction": true});
            skLineSegment(sketch, "E93.1.0.0", {"start": v(-18275, 2850) * mm, "end": v(-18275, 1650) * mm});
            skLineSegment(sketch, "E93.1.0.1", {"start": v(-20975, 2850) * mm, "end": v(-18275, 2850) * mm});
            skLineSegment(sketch, "E93.1.0.2", {"start": v(-20975, 2850) * mm, "end": v(-20975, 1650) * mm});
            skLineSegment(sketch, "E93.1.0.3", {"start": v(-20975, 1650) * mm, "end": v(-18275, 1650) * mm});
            skLineSegment(sketch, "E93.direction1", {"start": v(-17975, 1650) * mm, "end": v(-20975, 1650) * mm, "construction": true});
            skSolve(sketch);
        }
        {
            var Q0;
            Q0=qSketchRegion(id+"F10",true);
            extrude(context, id + "F11", {"entities" : qUnion([Q0]), "operationType" : NewBodyOperationType.REMOVE, "oppositeDirection" : true, "depth" : 300 * mm, "offsetDistance" : 25 * mm});
        }
        {
            var Q0;
            Q0=makeQuery(id+"F3.opExtrude","SWEPT_FACE",FACE,{"disambiguationData":[OSD([sQuery(id+"F2.wireOp",EDGE,"E2.1")])]});
            var sketch = newSketch(context, id + "F12", { "sketchPlane" : qUnion([Q0])});
            skLineSegment(sketch, "E94.0", {"start": v(17975, 2850) * mm, "end": v(15275, 2850) * mm});
            skLineSegment(sketch, "E94.1", {"start": v(17975, 1650) * mm, "end": v(15275, 1650) * mm});
            skLineSegment(sketch, "E94.2", {"start": v(17975, 2850) * mm, "end": v(17975, 1650) * mm});
            skLineSegment(sketch, "E94.3", {"start": v(15275, 2850) * mm, "end": v(15275, 1650) * mm});
            skLineSegment(sketch, "E94.4", {"start": v(12275, 2850) * mm, "end": v(12275, 1650) * mm});
            skLineSegment(sketch, "E94.5", {"start": v(14975, 2850) * mm, "end": v(14975, 1650) * mm});
            skLineSegment(sketch, "E94.6", {"start": v(14975, 1650) * mm, "end": v(12275, 1650) * mm});
            skLineSegment(sketch, "E94.7", {"start": v(14975, 2850) * mm, "end": v(12275, 2850) * mm});
            skLineSegment(sketch, "E94.8", {"start": v(9275, 2850) * mm, "end": v(9275, 1650) * mm});
            skLineSegment(sketch, "E94.9", {"start": v(11975, 2850) * mm, "end": v(11975, 1650) * mm});
            skLineSegment(sketch, "E94.10", {"start": v(11975, 1650) * mm, "end": v(9275, 1650) * mm});
            skLineSegment(sketch, "E94.11", {"start": v(11975, 2850) * mm, "end": v(9275, 2850) * mm});
            skLineSegment(sketch, "E94.12", {"start": v(6275, 2850) * mm, "end": v(6275, 1650) * mm});
            skLineSegment(sketch, "E94.13", {"start": v(8975, 2850) * mm, "end": v(8975, 1650) * mm});
            skLineSegment(sketch, "E94.14", {"start": v(8975, 1650) * mm, "end": v(6275, 1650) * mm});
            skLineSegment(sketch, "E94.15", {"start": v(8975, 2850) * mm, "end": v(6275, 2850) * mm});
            skLineSegment(sketch, "E94.16", {"start": v(17975, 1650) * mm, "end": v(14975, 1650) * mm});
            skLineSegment(sketch, "E95.0", {"start": v(20975, 2850) * mm, "end": v(18275, 2850) * mm});
            skLineSegment(sketch, "E96.0", {"start": v(18275, 2850) * mm, "end": v(18275, 1650) * mm});
            skLineSegment(sketch, "E97.0", {"start": v(20975, 1650) * mm, "end": v(18275, 1650) * mm});
            skLineSegment(sketch, "E98.0", {"start": v(20975, 2850) * mm, "end": v(20975, 1650) * mm});
            skSolve(sketch);
        }
        {
            var Q0;
            Q0=qSketchRegion(id+"F12",true);
            extrude(context, id + "F13", {"entities" : qUnion([Q0]), "oppositeDirection" : true, "depth" : 50 * mm, "offsetDistance" : 25 * mm});
        }
        {
            var Q0;
            Q0=makeQuery(id+"F13.opExtrude","CAP_FACE",FACE,{"disambiguationData":[OSD([sQuery(id+"F12.wireOp",EDGE,"E94.0"),sQuery(id+"F12.wireOp",EDGE,"E94.2"),sQuery(id+"F12.wireOp",EDGE,"E94.3"),sQuery(id+"F12.wireOp",EDGE,"E94.16")])],"isStart":false});
            var sketch = newSketch(context, id + "F14", { "sketchPlane" : qUnion([Q0])});
            skLineSegment(sketch, "E99.bottom", {"start": v(-17925, 2800) * mm, "end": v(-17325, 2800) * mm});
            skLineSegment(sketch, "E99.top", {"start": v(-17925, 1700) * mm, "end": v(-17325, 1700) * mm});
            skLineSegment(sketch, "E99.left", {"start": v(-17925, 2800) * mm, "end": v(-17925, 1700) * mm});
            skLineSegment(sketch, "E99.right", {"start": v(-17325, 2800) * mm, "end": v(-17325, 1700) * mm});
            skLineSegment(sketch, "E100", {"start": v(-16625, 1650) * mm, "end": v(-16625, 2850) * mm, "construction": true});
            skLineSegment(sketch, "E101.MirrorCS", {"start": v(-15925, 2800) * mm, "end": v(-15925, 1700) * mm});
            skLineSegment(sketch, "E102.MirrorCS", {"start": v(-15325, 2800) * mm, "end": v(-15325, 1700) * mm});
            skLineSegment(sketch, "E103.MirrorCS", {"start": v(-15325, 1700) * mm, "end": v(-15925, 1700) * mm});
            skLineSegment(sketch, "E104.MirrorCS", {"start": v(-15325, 2800) * mm, "end": v(-15925, 2800) * mm});
            skLineSegment(sketch, "E105.0.0", {"start": v(-17975, 2850) * mm, "end": v(-17975, 1650) * mm});
            skLineSegment(sketch, "E105.0.1", {"start": v(-17975, 1650) * mm, "end": v(-15275, 1650) * mm});
            skLineSegment(sketch, "E105.0.2", {"start": v(-15275, 1650) * mm, "end": v(-15275, 2850) * mm});
            skLineSegment(sketch, "E105.0.3", {"start": v(-15275, 2850) * mm, "end": v(-17975, 2850) * mm});
            skLineSegment(sketch, "E106.bottom", {"start": v(-17250, 2800) * mm, "end": v(-16000, 2800) * mm});
            skLineSegment(sketch, "E106.top", {"start": v(-17250, 1700) * mm, "end": v(-16000, 1700) * mm});
            skLineSegment(sketch, "E106.left", {"start": v(-17250, 2800) * mm, "end": v(-17250, 1700) * mm});
            skLineSegment(sketch, "E106.right", {"start": v(-16000, 2800) * mm, "end": v(-16000, 1700) * mm});
            skLineSegment(sketch, "E107.1.0.0", {"start": v(-13625, 1650) * mm, "end": v(-13625, 2850) * mm, "construction": true});
            skLineSegment(sketch, "E107.1.0.1", {"start": v(-12325, 2800) * mm, "end": v(-12925, 2800) * mm});
            skLineSegment(sketch, "E107.1.0.2", {"start": v(-12325, 1700) * mm, "end": v(-12925, 1700) * mm});
            skLineSegment(sketch, "E107.1.0.3", {"start": v(-12325, 2800) * mm, "end": v(-12325, 1700) * mm});
            skLineSegment(sketch, "E107.1.0.4", {"start": v(-12925, 2800) * mm, "end": v(-12925, 1700) * mm});
            skLineSegment(sketch, "E107.1.0.5", {"start": v(-14975, 2850) * mm, "end": v(-14975, 1650) * mm});
            skLineSegment(sketch, "E107.1.0.6", {"start": v(-14975, 1650) * mm, "end": v(-12275, 1650) * mm});
            skLineSegment(sketch, "E107.1.0.7", {"start": v(-13000, 2800) * mm, "end": v(-13000, 1700) * mm});
            skLineSegment(sketch, "E107.1.0.8", {"start": v(-12275, 1650) * mm, "end": v(-12275, 2850) * mm});
            skLineSegment(sketch, "E107.1.0.9", {"start": v(-12275, 2850) * mm, "end": v(-14975, 2850) * mm});
            skLineSegment(sketch, "E107.1.0.10", {"start": v(-14325, 2800) * mm, "end": v(-14325, 1700) * mm});
            skLineSegment(sketch, "E107.1.0.11", {"start": v(-14925, 2800) * mm, "end": v(-14925, 1700) * mm});
            skLineSegment(sketch, "E107.1.0.12", {"start": v(-14925, 1700) * mm, "end": v(-14325, 1700) * mm});
            skLineSegment(sketch, "E107.1.0.13", {"start": v(-14250, 1700) * mm, "end": v(-13000, 1700) * mm});
            skLineSegment(sketch, "E107.1.0.14", {"start": v(-14925, 2800) * mm, "end": v(-14325, 2800) * mm});
            skLineSegment(sketch, "E107.1.0.15", {"start": v(-14250, 2800) * mm, "end": v(-13000, 2800) * mm});
            skLineSegment(sketch, "E107.1.0.16", {"start": v(-14250, 2800) * mm, "end": v(-14250, 1700) * mm});
            skLineSegment(sketch, "E107.2.0.0", {"start": v(-10625, 1650) * mm, "end": v(-10625, 2850) * mm, "construction": true});
            skLineSegment(sketch, "E107.2.0.1", {"start": v(-9325, 2800) * mm, "end": v(-9925, 2800) * mm});
            skLineSegment(sketch, "E107.2.0.2", {"start": v(-9325, 1700) * mm, "end": v(-9925, 1700) * mm});
            skLineSegment(sketch, "E107.2.0.3", {"start": v(-9325, 2800) * mm, "end": v(-9325, 1700) * mm});
            skLineSegment(sketch, "E107.2.0.4", {"start": v(-9925, 2800) * mm, "end": v(-9925, 1700) * mm});
            skLineSegment(sketch, "E107.2.0.5", {"start": v(-11975, 2850) * mm, "end": v(-11975, 1650) * mm});
            skLineSegment(sketch, "E107.2.0.6", {"start": v(-11975, 1650) * mm, "end": v(-9275, 1650) * mm});
            skLineSegment(sketch, "E107.2.0.7", {"start": v(-10000, 2800) * mm, "end": v(-10000, 1700) * mm});
            skLineSegment(sketch, "E107.2.0.8", {"start": v(-9275, 1650) * mm, "end": v(-9275, 2850) * mm});
            skLineSegment(sketch, "E107.2.0.9", {"start": v(-9275, 2850) * mm, "end": v(-11975, 2850) * mm});
            skLineSegment(sketch, "E107.2.0.10", {"start": v(-11325, 2800) * mm, "end": v(-11325, 1700) * mm});
            skLineSegment(sketch, "E107.2.0.11", {"start": v(-11925, 2800) * mm, "end": v(-11925, 1700) * mm});
            skLineSegment(sketch, "E107.2.0.12", {"start": v(-11925, 1700) * mm, "end": v(-11325, 1700) * mm});
            skLineSegment(sketch, "E107.2.0.13", {"start": v(-11250, 1700) * mm, "end": v(-10000, 1700) * mm});
            skLineSegment(sketch, "E107.2.0.14", {"start": v(-11925, 2800) * mm, "end": v(-11325, 2800) * mm});
            skLineSegment(sketch, "E107.2.0.15", {"start": v(-11250, 2800) * mm, "end": v(-10000, 2800) * mm});
            skLineSegment(sketch, "E107.2.0.16", {"start": v(-11250, 2800) * mm, "end": v(-11250, 1700) * mm});
            skLineSegment(sketch, "E107.3.0.0", {"start": v(-7625, 1650) * mm, "end": v(-7625, 2850) * mm, "construction": true});
            skLineSegment(sketch, "E107.3.0.1", {"start": v(-6325, 2800) * mm, "end": v(-6925, 2800) * mm});
            skLineSegment(sketch, "E107.3.0.2", {"start": v(-6325, 1700) * mm, "end": v(-6925, 1700) * mm});
            skLineSegment(sketch, "E107.3.0.3", {"start": v(-6325, 2800) * mm, "end": v(-6325, 1700) * mm});
            skLineSegment(sketch, "E107.3.0.4", {"start": v(-6925, 2800) * mm, "end": v(-6925, 1700) * mm});
            skLineSegment(sketch, "E107.3.0.5", {"start": v(-8975, 2850) * mm, "end": v(-8975, 1650) * mm});
            skLineSegment(sketch, "E107.3.0.6", {"start": v(-8975, 1650) * mm, "end": v(-6275, 1650) * mm});
            skLineSegment(sketch, "E107.3.0.7", {"start": v(-7000, 2800) * mm, "end": v(-7000, 1700) * mm});
            skLineSegment(sketch, "E107.3.0.8", {"start": v(-6275, 1650) * mm, "end": v(-6275, 2850) * mm});
            skLineSegment(sketch, "E107.3.0.9", {"start": v(-6275, 2850) * mm, "end": v(-8975, 2850) * mm});
            skLineSegment(sketch, "E107.3.0.10", {"start": v(-8325, 2800) * mm, "end": v(-8325, 1700) * mm});
            skLineSegment(sketch, "E107.3.0.11", {"start": v(-8925, 2800) * mm, "end": v(-8925, 1700) * mm});
            skLineSegment(sketch, "E107.3.0.12", {"start": v(-8925, 1700) * mm, "end": v(-8325, 1700) * mm});
            skLineSegment(sketch, "E107.3.0.13", {"start": v(-8250, 1700) * mm, "end": v(-7000, 1700) * mm});
            skLineSegment(sketch, "E107.3.0.14", {"start": v(-8925, 2800) * mm, "end": v(-8325, 2800) * mm});
            skLineSegment(sketch, "E107.3.0.15", {"start": v(-8250, 2800) * mm, "end": v(-7000, 2800) * mm});
            skLineSegment(sketch, "E107.3.0.16", {"start": v(-8250, 2800) * mm, "end": v(-8250, 1700) * mm});
            skLineSegment(sketch, "E107.direction1", {"start": v(-17975, 1650) * mm, "end": v(-14975, 1650) * mm, "construction": true});
            skLineSegment(sketch, "E108.1.0.0", {"start": v(-20925, 2800) * mm, "end": v(-20325, 2800) * mm});
            skLineSegment(sketch, "E108.1.0.1", {"start": v(-18275, 2850) * mm, "end": v(-20975, 2850) * mm});
            skLineSegment(sketch, "E108.1.0.2", {"start": v(-20925, 2800) * mm, "end": v(-20925, 1700) * mm});
            skLineSegment(sketch, "E108.1.0.3", {"start": v(-20250, 2800) * mm, "end": v(-19000, 2800) * mm});
            skLineSegment(sketch, "E108.1.0.4", {"start": v(-20975, 2850) * mm, "end": v(-20975, 1650) * mm});
            skLineSegment(sketch, "E108.1.0.5", {"start": v(-18275, 1650) * mm, "end": v(-18275, 2850) * mm});
            skLineSegment(sketch, "E108.1.0.6", {"start": v(-20325, 2800) * mm, "end": v(-20325, 1700) * mm});
            skLineSegment(sketch, "E108.1.0.7", {"start": v(-18925, 2800) * mm, "end": v(-18925, 1700) * mm});
            skLineSegment(sketch, "E108.1.0.8", {"start": v(-18325, 2800) * mm, "end": v(-18925, 2800) * mm});
            skLineSegment(sketch, "E108.1.0.9", {"start": v(-20250, 2800) * mm, "end": v(-20250, 1700) * mm});
            skLineSegment(sketch, "E108.1.0.10", {"start": v(-20250, 1700) * mm, "end": v(-19000, 1700) * mm});
            skLineSegment(sketch, "E108.1.0.11", {"start": v(-19000, 2800) * mm, "end": v(-19000, 1700) * mm});
            skLineSegment(sketch, "E108.1.0.12", {"start": v(-20975, 1650) * mm, "end": v(-18275, 1650) * mm});
            skLineSegment(sketch, "E108.1.0.13", {"start": v(-18325, 2800) * mm, "end": v(-18325, 1700) * mm});
            skLineSegment(sketch, "E108.1.0.14", {"start": v(-18325, 1700) * mm, "end": v(-18925, 1700) * mm});
            skLineSegment(sketch, "E108.1.0.15", {"start": v(-20925, 1700) * mm, "end": v(-20325, 1700) * mm});
            skLineSegment(sketch, "E108.1.0.16", {"start": v(-19625, 1650) * mm, "end": v(-19625, 2850) * mm, "construction": true});
            skLineSegment(sketch, "E108.direction1", {"start": v(-17975, 1650) * mm, "end": v(-20975, 1650) * mm, "construction": true});
            skSolve(sketch);
        }
        {
            var Q0;
            Q0=qSketchRegion(id+"F14",true);
            extrude(context, id + "F15", {"entities" : qUnion([Q0]), "depth" : 50 * mm, "offsetDistance" : 25 * mm});
        }
        {
            var Q0;
            Q0=makeQuery(id+"F3.boolean.opBoolean","MERGE",FACE,{"derivedFrom":[makeQuery(id+"F1.opExtrude","SWEPT_FACE",FACE,{"disambiguationData":[OSD([sQuery(id+"F0.wireOp",EDGE,"E0.left")])]}),makeQuery(id+"F3.opExtrude","SWEPT_FACE",FACE,{"disambiguationData":[OSD([sQuery(id+"F2.wireOp",EDGE,"E1.0.0")])]})]});
            var sketch = newSketch(context, id + "F16", { "sketchPlane" : qUnion([Q0])});
            skLineSegment(sketch, "E109.bottom", {"start": v(250, 2850) * mm, "end": v(2950, 2850) * mm});
            skLineSegment(sketch, "E109.top", {"start": v(250, 1450) * mm, "end": v(2950, 1450) * mm});
            skLineSegment(sketch, "E109.left", {"start": v(250, 2850) * mm, "end": v(250, 1450) * mm});
            skLineSegment(sketch, "E109.right", {"start": v(2950, 2850) * mm, "end": v(2950, 1450) * mm});
            skLineSegment(sketch, "E110.bottom", {"start": v(3250, 2850) * mm, "end": v(5950, 2850) * mm});
            skLineSegment(sketch, "E110.top", {"start": v(3250, 1450) * mm, "end": v(5950, 1450) * mm});
            skLineSegment(sketch, "E110.left", {"start": v(3250, 2850) * mm, "end": v(3250, 1450) * mm});
            skLineSegment(sketch, "E110.right", {"start": v(5950, 2850) * mm, "end": v(5950, 1450) * mm});
            skSolve(sketch);
        }
        {
            var Q0;
            Q0=qSketchRegion(id+"F16",true);
            extrude(context, id + "F17", {"entities" : qUnion([Q0]), "operationType" : NewBodyOperationType.REMOVE, "oppositeDirection" : true, "depth" : 300 * mm, "offsetDistance" : 25 * mm});
        }
        {
            var Q0;
            Q0=makeQuery(id+"F5.boolean.opBoolean","MERGE",FACE,{"derivedFrom":[makeQuery(id+"F3.opExtrude","SWEPT_FACE",FACE,{"disambiguationData":[OSD([sQuery(id+"F2.wireOp",EDGE,"E2.0")])]}),makeQuery(id+"F5.opExtrude","SWEPT_FACE",FACE,{"disambiguationData":[OSD([sQuery(id+"F4.wireOp",EDGE,"E4")])]})]});
            var sketch = newSketch(context, id + "F18", { "sketchPlane" : qUnion([Q0])});
            skLineSegment(sketch, "E111.0", {"start": v(-250, 2850) * mm, "end": v(-2950, 2850) * mm});
            skLineSegment(sketch, "E111.1", {"start": v(-250, 1450) * mm, "end": v(-2950, 1450) * mm});
            skLineSegment(sketch, "E111.2", {"start": v(-250, 2850) * mm, "end": v(-250, 1450) * mm});
            skLineSegment(sketch, "E111.3", {"start": v(-2950, 2850) * mm, "end": v(-2950, 1450) * mm});
            skLineSegment(sketch, "E111.4", {"start": v(-3250, 2850) * mm, "end": v(-5950, 2850) * mm});
            skLineSegment(sketch, "E111.5", {"start": v(-3250, 1450) * mm, "end": v(-5950, 1450) * mm});
            skLineSegment(sketch, "E111.6", {"start": v(-3250, 2850) * mm, "end": v(-3250, 1450) * mm});
            skLineSegment(sketch, "E111.7", {"start": v(-5950, 2850) * mm, "end": v(-5950, 1450) * mm});
            skSolve(sketch);
        }
        {
            var Q0;
            Q0=qSketchRegion(id+"F18",true);
            extrude(context, id + "F19", {"entities" : qUnion([Q0]), "oppositeDirection" : true, "depth" : 50 * mm, "offsetDistance" : 25 * mm});
        }
        {
            var Q0;
            Q0=makeQuery(id+"F19.opExtrude","CAP_FACE",FACE,{"disambiguationData":[OSD([sQuery(id+"F18.wireOp",EDGE,"E111.0"),sQuery(id+"F18.wireOp",EDGE,"E111.1"),sQuery(id+"F18.wireOp",EDGE,"E111.2"),sQuery(id+"F18.wireOp",EDGE,"E111.3")])],"isStart":false});
            var sketch = newSketch(context, id + "F20", { "sketchPlane" : qUnion([Q0])});
            skLineSegment(sketch, "E112.0.0", {"start": v(250, 2850) * mm, "end": v(250, 1450) * mm});
            skLineSegment(sketch, "E112.0.1", {"start": v(250, 1450) * mm, "end": v(2950, 1450) * mm});
            skLineSegment(sketch, "E112.0.2", {"start": v(2950, 1450) * mm, "end": v(2950, 2850) * mm});
            skLineSegment(sketch, "E112.0.3", {"start": v(2950, 2850) * mm, "end": v(250, 2850) * mm});
            skLineSegment(sketch, "E113.bottom", {"start": v(300, 2800) * mm, "end": v(1100, 2800) * mm});
            skLineSegment(sketch, "E113.top", {"start": v(300, 1500) * mm, "end": v(1100, 1500) * mm});
            skLineSegment(sketch, "E113.left", {"start": v(300, 2800) * mm, "end": v(300, 1500) * mm});
            skLineSegment(sketch, "E113.right", {"start": v(1100, 2800) * mm, "end": v(1100, 1500) * mm});
            skLineSegment(sketch, "E114.bottom", {"start": v(1150, 2800) * mm, "end": v(2050, 2800) * mm});
            skLineSegment(sketch, "E114.top", {"start": v(1150, 1500) * mm, "end": v(2050, 1500) * mm});
            skLineSegment(sketch, "E114.left", {"start": v(1150, 2800) * mm, "end": v(1150, 1500) * mm});
            skLineSegment(sketch, "E114.right", {"start": v(2050, 2800) * mm, "end": v(2050, 1500) * mm});
            skLineSegment(sketch, "E115.bottom", {"start": v(2100, 2800) * mm, "end": v(2900, 2800) * mm});
            skLineSegment(sketch, "E115.top", {"start": v(2100, 1500) * mm, "end": v(2900, 1500) * mm});
            skLineSegment(sketch, "E115.left", {"start": v(2100, 2800) * mm, "end": v(2100, 1500) * mm});
            skLineSegment(sketch, "E115.right", {"start": v(2900, 2800) * mm, "end": v(2900, 1500) * mm});
            skLineSegment(sketch, "E116.1.0.0", {"start": v(5100, 2800) * mm, "end": v(5100, 1500) * mm});
            skLineSegment(sketch, "E116.1.0.1", {"start": v(5100, 1500) * mm, "end": v(5900, 1500) * mm});
            skLineSegment(sketch, "E116.1.0.2", {"start": v(5900, 2800) * mm, "end": v(5900, 1500) * mm});
            skLineSegment(sketch, "E116.1.0.3", {"start": v(4100, 2800) * mm, "end": v(4100, 1500) * mm});
            skLineSegment(sketch, "E116.1.0.4", {"start": v(5050, 2800) * mm, "end": v(5050, 1500) * mm});
            skLineSegment(sketch, "E116.1.0.5", {"start": v(4150, 1500) * mm, "end": v(5050, 1500) * mm});
            skLineSegment(sketch, "E116.1.0.6", {"start": v(4150, 2800) * mm, "end": v(5050, 2800) * mm});
            skLineSegment(sketch, "E116.1.0.7", {"start": v(3250, 1450) * mm, "end": v(5950, 1450) * mm});
            skLineSegment(sketch, "E116.1.0.8", {"start": v(5100, 2800) * mm, "end": v(5900, 2800) * mm});
            skLineSegment(sketch, "E116.1.0.9", {"start": v(4150, 2800) * mm, "end": v(4150, 1500) * mm});
            skLineSegment(sketch, "E116.1.0.10", {"start": v(5950, 1450) * mm, "end": v(5950, 2850) * mm});
            skLineSegment(sketch, "E116.1.0.11", {"start": v(5950, 2850) * mm, "end": v(3250, 2850) * mm});
            skLineSegment(sketch, "E116.1.0.12", {"start": v(3300, 2800) * mm, "end": v(4100, 2800) * mm});
            skLineSegment(sketch, "E116.1.0.13", {"start": v(3300, 1500) * mm, "end": v(4100, 1500) * mm});
            skLineSegment(sketch, "E116.1.0.14", {"start": v(3300, 2800) * mm, "end": v(3300, 1500) * mm});
            skLineSegment(sketch, "E116.1.0.15", {"start": v(3250, 2850) * mm, "end": v(3250, 1450) * mm});
            skLineSegment(sketch, "E116.direction1", {"start": v(250, 1450) * mm, "end": v(3250, 1450) * mm, "construction": true});
            skSolve(sketch);
        }
        {
            var Q0;
            Q0=qSketchRegion(id+"F20",true);
            extrude(context, id + "F21", {"entities" : qUnion([Q0]), "depth" : 50 * mm, "offsetDistance" : 25 * mm});
        }
        {
            var Q0;
            Q0=makeQuery(id+"F3.boolean.opBoolean","MERGE",FACE,{"derivedFrom":[makeQuery(id+"F1.opExtrude","SWEPT_FACE",FACE,{"disambiguationData":[OSD([sQuery(id+"F0.wireOp",EDGE,"E0.top")])]}),makeQuery(id+"F3.opExtrude","SWEPT_FACE",FACE,{"disambiguationData":[OSD([sQuery(id+"F2.wireOp",EDGE,"E1.0.1")])]})]});
            var sketch = newSketch(context, id + "F22", { "sketchPlane" : qUnion([Q0])});
            skLineSegment(sketch, "E117.bottom", {"start": v(0, 0) * mm, "end": v(18250, 0) * mm});
            skLineSegment(sketch, "E117.top", {"start": v(0, 150) * mm, "end": v(18250, 150) * mm});
            skLineSegment(sketch, "E117.left", {"start": v(0, 0) * mm, "end": v(0, 150) * mm});
            skLineSegment(sketch, "E117.right", {"start": v(18250, 0) * mm, "end": v(18250, 150) * mm});
            skSolve(sketch);
        }
        {
            var Q0;
            Q0 = qSketchRegion(id + "F22", true);
            extrude(context, id + "F23", {"entities" : qUnion([Q0]), "operationType" : NewBodyOperationType.ADD, "depth" : 1800 * mm, "offsetDistance" : 25 * mm});
        }
        {
            var Q0;
            Q0=makeQuery(id+"F23.boolean.opBoolean","MERGE",FACE,{"derivedFrom":[makeQuery(id+"F5.boolean.opBoolean","MERGE",FACE,{"derivedFrom":[makeQuery(id+"F1.opExtrude","CAP_FACE",FACE,{"disambiguationData":[OSD([sQuery(id+"F0.wireOp",EDGE,"E0.bottom"),sQuery(id+"F0.wireOp",EDGE,"E0.top"),sQuery(id+"F0.wireOp",EDGE,"E0.left"),sQuery(id+"F0.wireOp",EDGE,"E0.right")])],"isStart":false}),makeQuery(id+"F5.opExtrude","SWEPT_FACE",FACE,{"disambiguationData":[OSD([sQuery(id+"F4.wireOp",EDGE,"E3")])]}),makeQuery(id+"F5.opExtrude","SWEPT_FACE",FACE,{"disambiguationData":[OSD([sQuery(id+"F4.wireOp",EDGE,"E17.MirrorCS")])]})]}),makeQuery(id+"F23.opExtrude","SWEPT_FACE",FACE,{"disambiguationData":[OSD([sQuery(id+"F22.wireOp",EDGE,"E117.top")])]})]});
            var sketch = newSketch(context, id + "F24", { "sketchPlane" : qUnion([Q0])});
            skLineSegment(sketch, "E118.0", {"start": v(0, -11050) * mm, "end": v(0, -9250) * mm});
            skLineSegment(sketch, "E119.0", {"start": v(0, -11050) * mm, "end": v(18250, -11050) * mm});
            skLineSegment(sketch, "E120.0", {"start": v(18250, -11050) * mm, "end": v(18250, -9250) * mm});
            skLineSegment(sketch, "E121.0", {"start": v(18150, -10950) * mm, "end": v(18150, -9250) * mm});
            skLineSegment(sketch, "E121.1", {"start": v(100, -10950) * mm, "end": v(18150, -10950) * mm});
            skLineSegment(sketch, "E121.2", {"start": v(100, -10950) * mm, "end": v(100, -9250) * mm});
            skLineSegment(sketch, "E122", {"start": v(0, -9250) * mm, "end": v(100, -9250) * mm});
            skLineSegment(sketch, "E123", {"start": v(18150, -9250) * mm, "end": v(18250, -9250) * mm});
            skSolve(sketch);
        }
        {
            var Q0;
            Q0 = qSketchRegion(id + "F24", true);
            extrude(context, id + "F25", {"entities" : qUnion([Q0]), "operationType" : NewBodyOperationType.ADD, "depth" : 600 * mm, "offsetDistance" : 25 * mm});
        }
        {
            var Q0;
            Q0=makeQuery(id+"F25.opExtrude","CAP_FACE",FACE,{"disambiguationData":[OSD([sQuery(id+"F24.wireOp",EDGE,"E118.0"),sQuery(id+"F24.wireOp",EDGE,"E119.0"),sQuery(id+"F24.wireOp",EDGE,"E120.0"),sQuery(id+"F24.wireOp",EDGE,"E121.0"),sQuery(id+"F24.wireOp",EDGE,"E121.1"),sQuery(id+"F24.wireOp",EDGE,"E121.2"),sQuery(id+"F24.wireOp",EDGE,"E122"),sQuery(id+"F24.wireOp",EDGE,"E123")])],"isStart":false});
            var sketch = newSketch(context, id + "F26", { "sketchPlane" : qUnion([Q0])});
            skLineSegment(sketch, "E124.bottom", {"start": v(0, -9250) * mm, "end": v(50, -9250) * mm});
            skLineSegment(sketch, "E124.top", {"start": v(0, -9300) * mm, "end": v(50, -9300) * mm});
            skLineSegment(sketch, "E124.left", {"start": v(0, -9250) * mm, "end": v(0, -9300) * mm});
            skLineSegment(sketch, "E124.right", {"start": v(50, -9250) * mm, "end": v(50, -9300) * mm});
            skLineSegment(sketch, "E125.0.1.0", {"start": v(0, -10170) * mm, "end": v(50, -10170) * mm});
            skLineSegment(sketch, "E125.0.1.1", {"start": v(50, -10120) * mm, "end": v(50, -10170) * mm});
            skLineSegment(sketch, "E125.0.1.2", {"start": v(0, -10120) * mm, "end": v(50, -10120) * mm});
            skLineSegment(sketch, "E125.0.1.3", {"start": v(0, -10120) * mm, "end": v(0, -10170) * mm});
            skLineSegment(sketch, "E125.0.2.0", {"start": v(0, -11040) * mm, "end": v(50, -11040) * mm});
            skLineSegment(sketch, "E125.0.2.1", {"start": v(50, -10990) * mm, "end": v(50, -11040) * mm});
            skLineSegment(sketch, "E125.0.2.2", {"start": v(0, -10990) * mm, "end": v(50, -10990) * mm});
            skLineSegment(sketch, "E125.0.2.3", {"start": v(0, -10990) * mm, "end": v(0, -11040) * mm});
            skLineSegment(sketch, "E125.direction1", {"start": v(0, -9300) * mm, "end": v(25, -9300) * mm, "construction": true});
            skLineSegment(sketch, "E125.direction2", {"start": v(0, -9300) * mm, "end": v(0, -10170) * mm, "construction": true});
            skLineSegment(sketch, "E126", {"start": v(9125, -11050) * mm, "end": v(9125, -9470.15) * mm, "construction": true});
            skLineSegment(sketch, "E127.MirrorCS", {"start": v(18250, -9300) * mm, "end": v(18200, -9300) * mm});
            skLineSegment(sketch, "E128.MirrorCS", {"start": v(18250, -10990) * mm, "end": v(18200, -10990) * mm});
            skLineSegment(sketch, "E129.MirrorCS", {"start": v(18250, -9300) * mm, "end": v(18225, -9300) * mm, "construction": true});
            skLineSegment(sketch, "E130.MirrorCS", {"start": v(18250, -11040) * mm, "end": v(18200, -11040) * mm});
            skLineSegment(sketch, "E131.MirrorCS", {"start": v(18200, -9250) * mm, "end": v(18200, -9300) * mm});
            skLineSegment(sketch, "E132.MirrorCS", {"start": v(18250, -10990) * mm, "end": v(18250, -11040) * mm});
            skLineSegment(sketch, "E133.MirrorCS", {"start": v(18250, -9250) * mm, "end": v(18200, -9250) * mm});
            skLineSegment(sketch, "E134.MirrorCS", {"start": v(18250, -9250) * mm, "end": v(18250, -9300) * mm});
            skLineSegment(sketch, "E135.MirrorCS", {"start": v(18250, -10170) * mm, "end": v(18200, -10170) * mm});
            skLineSegment(sketch, "E136.MirrorCS", {"start": v(18200, -10990) * mm, "end": v(18200, -11040) * mm});
            skLineSegment(sketch, "E137.MirrorCS", {"start": v(18200, -10120) * mm, "end": v(18200, -10170) * mm});
            skLineSegment(sketch, "E138.MirrorCS", {"start": v(18250, -10120) * mm, "end": v(18250, -10170) * mm});
            skLineSegment(sketch, "E139.MirrorCS", {"start": v(18250, -10120) * mm, "end": v(18200, -10120) * mm});
            skLineSegment(sketch, "E140.MirrorCS", {"start": v(18250, -9300) * mm, "end": v(18250, -10170) * mm, "construction": true});
            skLineSegment(sketch, "E141.1.0.0", {"start": v(870, -11040) * mm, "end": v(920, -11040) * mm});
            skLineSegment(sketch, "E141.1.0.1", {"start": v(920, -10990) * mm, "end": v(920, -11040) * mm});
            skLineSegment(sketch, "E141.1.0.2", {"start": v(870, -10990) * mm, "end": v(920, -10990) * mm});
            skLineSegment(sketch, "E141.1.0.3", {"start": v(870, -10990) * mm, "end": v(870, -11040) * mm});
            skLineSegment(sketch, "E141.2.0.0", {"start": v(1740, -11040) * mm, "end": v(1790, -11040) * mm});
            skLineSegment(sketch, "E141.2.0.1", {"start": v(1790, -10990) * mm, "end": v(1790, -11040) * mm});
            skLineSegment(sketch, "E141.2.0.2", {"start": v(1740, -10990) * mm, "end": v(1790, -10990) * mm});
            skLineSegment(sketch, "E141.2.0.3", {"start": v(1740, -10990) * mm, "end": v(1740, -11040) * mm});
            skLineSegment(sketch, "E141.3.0.0", {"start": v(2610, -11040) * mm, "end": v(2660, -11040) * mm});
            skLineSegment(sketch, "E141.3.0.1", {"start": v(2660, -10990) * mm, "end": v(2660, -11040) * mm});
            skLineSegment(sketch, "E141.3.0.2", {"start": v(2610, -10990) * mm, "end": v(2660, -10990) * mm});
            skLineSegment(sketch, "E141.3.0.3", {"start": v(2610, -10990) * mm, "end": v(2610, -11040) * mm});
            skLineSegment(sketch, "E141.4.0.0", {"start": v(3480, -11040) * mm, "end": v(3530, -11040) * mm});
            skLineSegment(sketch, "E141.4.0.1", {"start": v(3530, -10990) * mm, "end": v(3530, -11040) * mm});
            skLineSegment(sketch, "E141.4.0.2", {"start": v(3480, -10990) * mm, "end": v(3530, -10990) * mm});
            skLineSegment(sketch, "E141.4.0.3", {"start": v(3480, -10990) * mm, "end": v(3480, -11040) * mm});
            skLineSegment(sketch, "E141.5.0.0", {"start": v(4350, -11040) * mm, "end": v(4400, -11040) * mm});
            skLineSegment(sketch, "E141.5.0.1", {"start": v(4400, -10990) * mm, "end": v(4400, -11040) * mm});
            skLineSegment(sketch, "E141.5.0.2", {"start": v(4350, -10990) * mm, "end": v(4400, -10990) * mm});
            skLineSegment(sketch, "E141.5.0.3", {"start": v(4350, -10990) * mm, "end": v(4350, -11040) * mm});
            skLineSegment(sketch, "E141.6.0.0", {"start": v(5220, -11040) * mm, "end": v(5270, -11040) * mm});
            skLineSegment(sketch, "E141.6.0.1", {"start": v(5270, -10990) * mm, "end": v(5270, -11040) * mm});
            skLineSegment(sketch, "E141.6.0.2", {"start": v(5220, -10990) * mm, "end": v(5270, -10990) * mm});
            skLineSegment(sketch, "E141.6.0.3", {"start": v(5220, -10990) * mm, "end": v(5220, -11040) * mm});
            skLineSegment(sketch, "E141.7.0.0", {"start": v(6090, -11040) * mm, "end": v(6140, -11040) * mm});
            skLineSegment(sketch, "E141.7.0.1", {"start": v(6140, -10990) * mm, "end": v(6140, -11040) * mm});
            skLineSegment(sketch, "E141.7.0.2", {"start": v(6090, -10990) * mm, "end": v(6140, -10990) * mm});
            skLineSegment(sketch, "E141.7.0.3", {"start": v(6090, -10990) * mm, "end": v(6090, -11040) * mm});
            skLineSegment(sketch, "E141.8.0.0", {"start": v(6960, -11040) * mm, "end": v(7010, -11040) * mm});
            skLineSegment(sketch, "E141.8.0.1", {"start": v(7010, -10990) * mm, "end": v(7010, -11040) * mm});
            skLineSegment(sketch, "E141.8.0.2", {"start": v(6960, -10990) * mm, "end": v(7010, -10990) * mm});
            skLineSegment(sketch, "E141.8.0.3", {"start": v(6960, -10990) * mm, "end": v(6960, -11040) * mm});
            skLineSegment(sketch, "E141.9.0.0", {"start": v(7830, -11040) * mm, "end": v(7880, -11040) * mm});
            skLineSegment(sketch, "E141.9.0.1", {"start": v(7880, -10990) * mm, "end": v(7880, -11040) * mm});
            skLineSegment(sketch, "E141.9.0.2", {"start": v(7830, -10990) * mm, "end": v(7880, -10990) * mm});
            skLineSegment(sketch, "E141.9.0.3", {"start": v(7830, -10990) * mm, "end": v(7830, -11040) * mm});
            skLineSegment(sketch, "E141.10.0.0", {"start": v(8700, -11040) * mm, "end": v(8750, -11040) * mm});
            skLineSegment(sketch, "E141.10.0.1", {"start": v(8750, -10990) * mm, "end": v(8750, -11040) * mm});
            skLineSegment(sketch, "E141.10.0.2", {"start": v(8700, -10990) * mm, "end": v(8750, -10990) * mm});
            skLineSegment(sketch, "E141.10.0.3", {"start": v(8700, -10990) * mm, "end": v(8700, -11040) * mm});
            skLineSegment(sketch, "E141.11.0.0", {"start": v(9570, -11040) * mm, "end": v(9620, -11040) * mm});
            skLineSegment(sketch, "E141.11.0.1", {"start": v(9620, -10990) * mm, "end": v(9620, -11040) * mm});
            skLineSegment(sketch, "E141.11.0.2", {"start": v(9570, -10990) * mm, "end": v(9620, -10990) * mm});
            skLineSegment(sketch, "E141.11.0.3", {"start": v(9570, -10990) * mm, "end": v(9570, -11040) * mm});
            skLineSegment(sketch, "E141.12.0.0", {"start": v(10440, -11040) * mm, "end": v(10490, -11040) * mm});
            skLineSegment(sketch, "E141.12.0.1", {"start": v(10490, -10990) * mm, "end": v(10490, -11040) * mm});
            skLineSegment(sketch, "E141.12.0.2", {"start": v(10440, -10990) * mm, "end": v(10490, -10990) * mm});
            skLineSegment(sketch, "E141.12.0.3", {"start": v(10440, -10990) * mm, "end": v(10440, -11040) * mm});
            skLineSegment(sketch, "E141.13.0.0", {"start": v(11310, -11040) * mm, "end": v(11360, -11040) * mm});
            skLineSegment(sketch, "E141.13.0.1", {"start": v(11360, -10990) * mm, "end": v(11360, -11040) * mm});
            skLineSegment(sketch, "E141.13.0.2", {"start": v(11310, -10990) * mm, "end": v(11360, -10990) * mm});
            skLineSegment(sketch, "E141.13.0.3", {"start": v(11310, -10990) * mm, "end": v(11310, -11040) * mm});
            skLineSegment(sketch, "E141.14.0.0", {"start": v(12180, -11040) * mm, "end": v(12230, -11040) * mm});
            skLineSegment(sketch, "E141.14.0.1", {"start": v(12230, -10990) * mm, "end": v(12230, -11040) * mm});
            skLineSegment(sketch, "E141.14.0.2", {"start": v(12180, -10990) * mm, "end": v(12230, -10990) * mm});
            skLineSegment(sketch, "E141.14.0.3", {"start": v(12180, -10990) * mm, "end": v(12180, -11040) * mm});
            skLineSegment(sketch, "E141.15.0.0", {"start": v(13050, -11040) * mm, "end": v(13100, -11040) * mm});
            skLineSegment(sketch, "E141.15.0.1", {"start": v(13100, -10990) * mm, "end": v(13100, -11040) * mm});
            skLineSegment(sketch, "E141.15.0.2", {"start": v(13050, -10990) * mm, "end": v(13100, -10990) * mm});
            skLineSegment(sketch, "E141.15.0.3", {"start": v(13050, -10990) * mm, "end": v(13050, -11040) * mm});
            skLineSegment(sketch, "E141.16.0.0", {"start": v(13920, -11040) * mm, "end": v(13970, -11040) * mm});
            skLineSegment(sketch, "E141.16.0.1", {"start": v(13970, -10990) * mm, "end": v(13970, -11040) * mm});
            skLineSegment(sketch, "E141.16.0.2", {"start": v(13920, -10990) * mm, "end": v(13970, -10990) * mm});
            skLineSegment(sketch, "E141.16.0.3", {"start": v(13920, -10990) * mm, "end": v(13920, -11040) * mm});
            skLineSegment(sketch, "E141.17.0.0", {"start": v(14790, -11040) * mm, "end": v(14840, -11040) * mm});
            skLineSegment(sketch, "E141.17.0.1", {"start": v(14840, -10990) * mm, "end": v(14840, -11040) * mm});
            skLineSegment(sketch, "E141.17.0.2", {"start": v(14790, -10990) * mm, "end": v(14840, -10990) * mm});
            skLineSegment(sketch, "E141.17.0.3", {"start": v(14790, -10990) * mm, "end": v(14790, -11040) * mm});
            skLineSegment(sketch, "E141.18.0.0", {"start": v(15660, -11040) * mm, "end": v(15710, -11040) * mm});
            skLineSegment(sketch, "E141.18.0.1", {"start": v(15710, -10990) * mm, "end": v(15710, -11040) * mm});
            skLineSegment(sketch, "E141.18.0.2", {"start": v(15660, -10990) * mm, "end": v(15710, -10990) * mm});
            skLineSegment(sketch, "E141.18.0.3", {"start": v(15660, -10990) * mm, "end": v(15660, -11040) * mm});
            skLineSegment(sketch, "E141.19.0.0", {"start": v(16530, -11040) * mm, "end": v(16580, -11040) * mm});
            skLineSegment(sketch, "E141.19.0.1", {"start": v(16580, -10990) * mm, "end": v(16580, -11040) * mm});
            skLineSegment(sketch, "E141.19.0.2", {"start": v(16530, -10990) * mm, "end": v(16580, -10990) * mm});
            skLineSegment(sketch, "E141.19.0.3", {"start": v(16530, -10990) * mm, "end": v(16530, -11040) * mm});
            skLineSegment(sketch, "E141.20.0.0", {"start": v(17400, -11040) * mm, "end": v(17450, -11040) * mm});
            skLineSegment(sketch, "E141.20.0.1", {"start": v(17450, -10990) * mm, "end": v(17450, -11040) * mm});
            skLineSegment(sketch, "E141.20.0.2", {"start": v(17400, -10990) * mm, "end": v(17450, -10990) * mm});
            skLineSegment(sketch, "E141.20.0.3", {"start": v(17400, -10990) * mm, "end": v(17400, -11040) * mm});
            skLineSegment(sketch, "E141.direction1", {"start": v(0, -11040) * mm, "end": v(870, -11040) * mm, "construction": true});
            skSolve(sketch);
        }
        {
            var Q0;
            Q0 = qSketchRegion(id + "F26", true);
            extrude(context, id + "F27", {"entities" : qUnion([Q0]), "depth" : 75 * mm, "offsetDistance" : 25 * mm});
        }
        {
            var Q0;
            Q0=makeQuery(id+"F27.opExtrude","CAP_FACE",FACE,{"disambiguationData":[OSD([sQuery(id+"F26.wireOp",EDGE,"E124.bottom"),sQuery(id+"F26.wireOp",EDGE,"E124.top"),sQuery(id+"F26.wireOp",EDGE,"E124.left"),sQuery(id+"F26.wireOp",EDGE,"E124.right")])],"isStart":false});
            var sketch = newSketch(context, id + "F28", { "sketchPlane" : qUnion([Q0])});
            skLineSegment(sketch, "E142.bottom", {"start": v(0, -9250) * mm, "end": v(50, -9250) * mm});
            skLineSegment(sketch, "E142.top", {"start": v(0, -11040) * mm, "end": v(50, -11040) * mm});
            skLineSegment(sketch, "E142.left", {"start": v(0, -9250) * mm, "end": v(0, -11040) * mm});
            skLineSegment(sketch, "E142.right", {"start": v(50, -9250) * mm, "end": v(50, -10990) * mm});
            skLineSegment(sketch, "E143.bottom", {"start": v(50, -11040) * mm, "end": v(18250, -11040) * mm});
            skLineSegment(sketch, "E143.top", {"start": v(50, -10990) * mm, "end": v(18200, -10990) * mm});
            skLineSegment(sketch, "E143.right", {"start": v(18250, -11040) * mm, "end": v(18250, -10990) * mm});
            skLineSegment(sketch, "E144.bottom", {"start": v(18200, -9250) * mm, "end": v(18250, -9250) * mm});
            skLineSegment(sketch, "E144.left", {"start": v(18200, -9250) * mm, "end": v(18200, -10990) * mm});
            skLineSegment(sketch, "E144.right", {"start": v(18250, -9250) * mm, "end": v(18250, -10990) * mm});
            skSolve(sketch);
        }
        {
            var Q0;
            Q0 = qSketchRegion(id + "F28", true);
            extrude(context, id + "F29", {"entities" : qUnion([Q0]), "depth" : 50 * mm, "offsetDistance" : 25 * mm});
        }
    });
